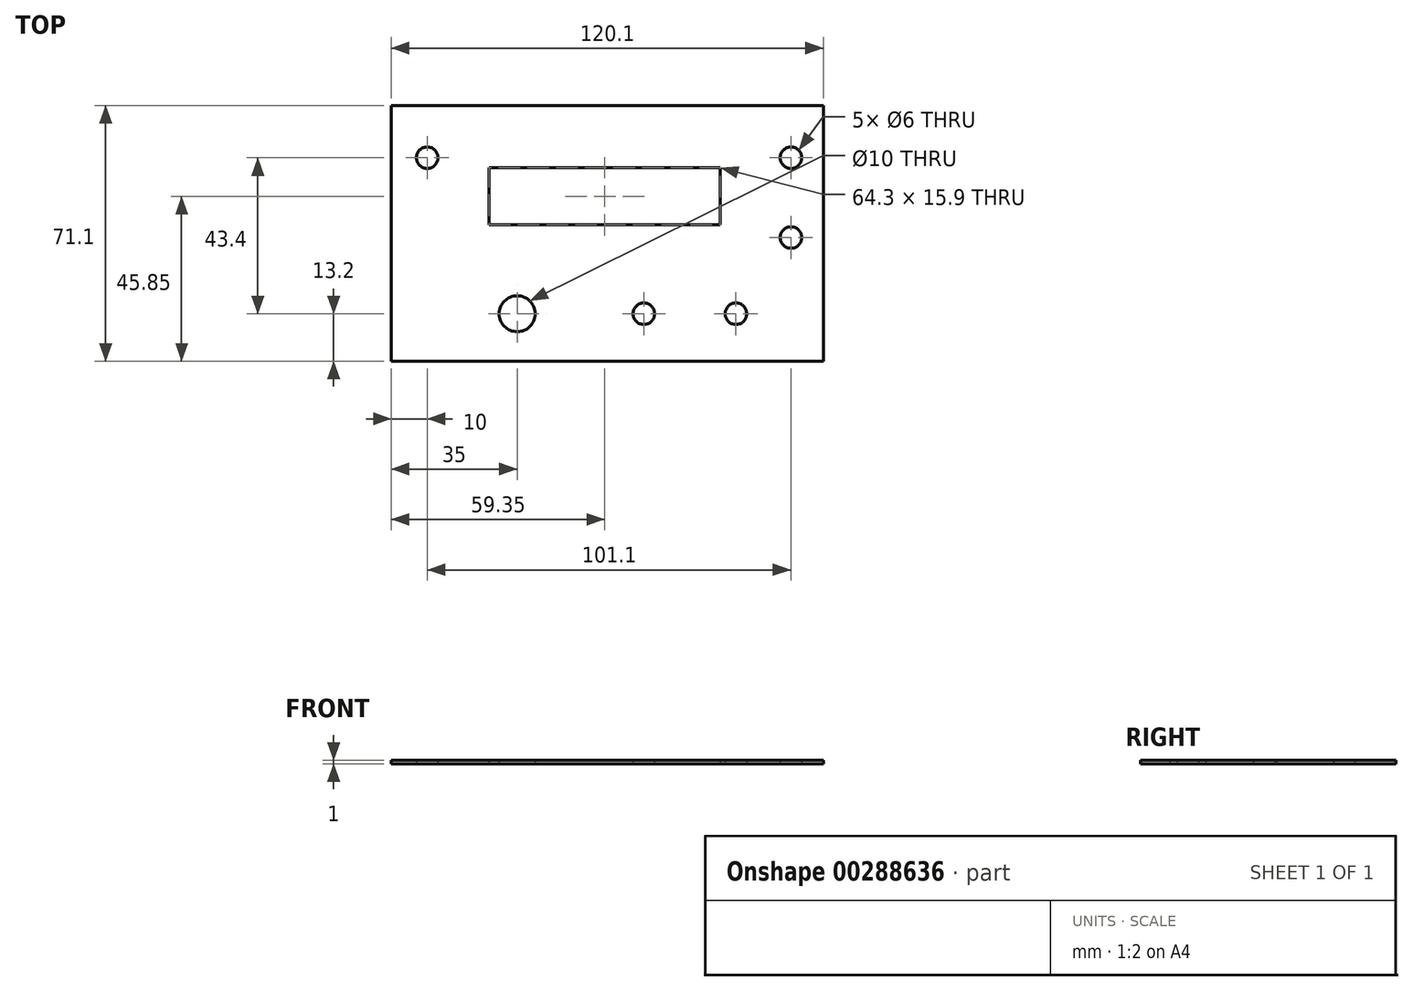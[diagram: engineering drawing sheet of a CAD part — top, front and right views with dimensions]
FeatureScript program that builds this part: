
annotation { "Feature Type Name" : "Feature", "Feature Type Description" : "" }
export const myFeature = defineFeature(function(context is Context, id is Id, definition is map)
    precondition{}
    {
        {
            var Q0;
            Q0=qCreatedBy(makeId("Top.planeOp"),FACE);
            var sketch = newSketch(context, id + "F0", { "sketchPlane" : qUnion([Q0])});
            skLineSegment(sketch, "E0.bottom", {"start": v(0, 0) * mm, "end": v(120.1, 0) * mm});
            skLineSegment(sketch, "E0.top", {"start": v(0, 71.1) * mm, "end": v(120.1, 71.1) * mm});
            skLineSegment(sketch, "E0.left", {"start": v(0, 0) * mm, "end": v(0, 71.1) * mm});
            skLineSegment(sketch, "E0.right", {"start": v(120.1, 0) * mm, "end": v(120.1, 71.1) * mm});
            skLineSegment(sketch, "E1.bottom", {"start": v(27.2, 53.8) * mm, "end": v(91.5, 53.8) * mm});
            skLineSegment(sketch, "E1.top", {"start": v(27.2, 37.9) * mm, "end": v(91.5, 37.9) * mm});
            skLineSegment(sketch, "E1.left", {"start": v(27.2, 53.8) * mm, "end": v(27.2, 37.9) * mm});
            skLineSegment(sketch, "E1.right", {"start": v(91.5, 53.8) * mm, "end": v(91.5, 37.9) * mm});
            skCircle(sketch, "E2", {"center": v(95.8, 13.2) * mm, "radius": 3 * mm});
            skCircle(sketch, "E3", {"center": v(70.2, 13.2) * mm, "radius": 3 * mm});
            skCircle(sketch, "E4", {"center": v(10, 56.6) * mm, "radius": 3 * mm});
            skCircle(sketch, "E5", {"center": v(111.1, 56.6) * mm, "radius": 3 * mm});
            skCircle(sketch, "E6", {"center": v(111.1, 34.4) * mm, "radius": 3 * mm});
            skCircle(sketch, "E7", {"center": v(35, 13.2) * mm, "radius": 5 * mm});
            skLineSegment(sketch, "E8", {"start": v(111.1, 80) * mm, "end": v(111.1, -17) * mm, "construction": true});
            skLineSegment(sketch, "E9", {"start": v(-39.26, 13.2) * mm, "end": v(139.07, 13.2) * mm, "construction": true});
            skLineSegment(sketch, "E10", {"start": v(10, 81.36) * mm, "end": v(10, -11.58) * mm, "construction": true});
            skSolve(sketch);
        }
        {
            var Q0;
            Q0 = qSketchRegion(id + "F0", true);
            extrude(context, id + "F1", {"entities" : qUnion([Q0]), "depth" : 1 * mm});
        }
    });
